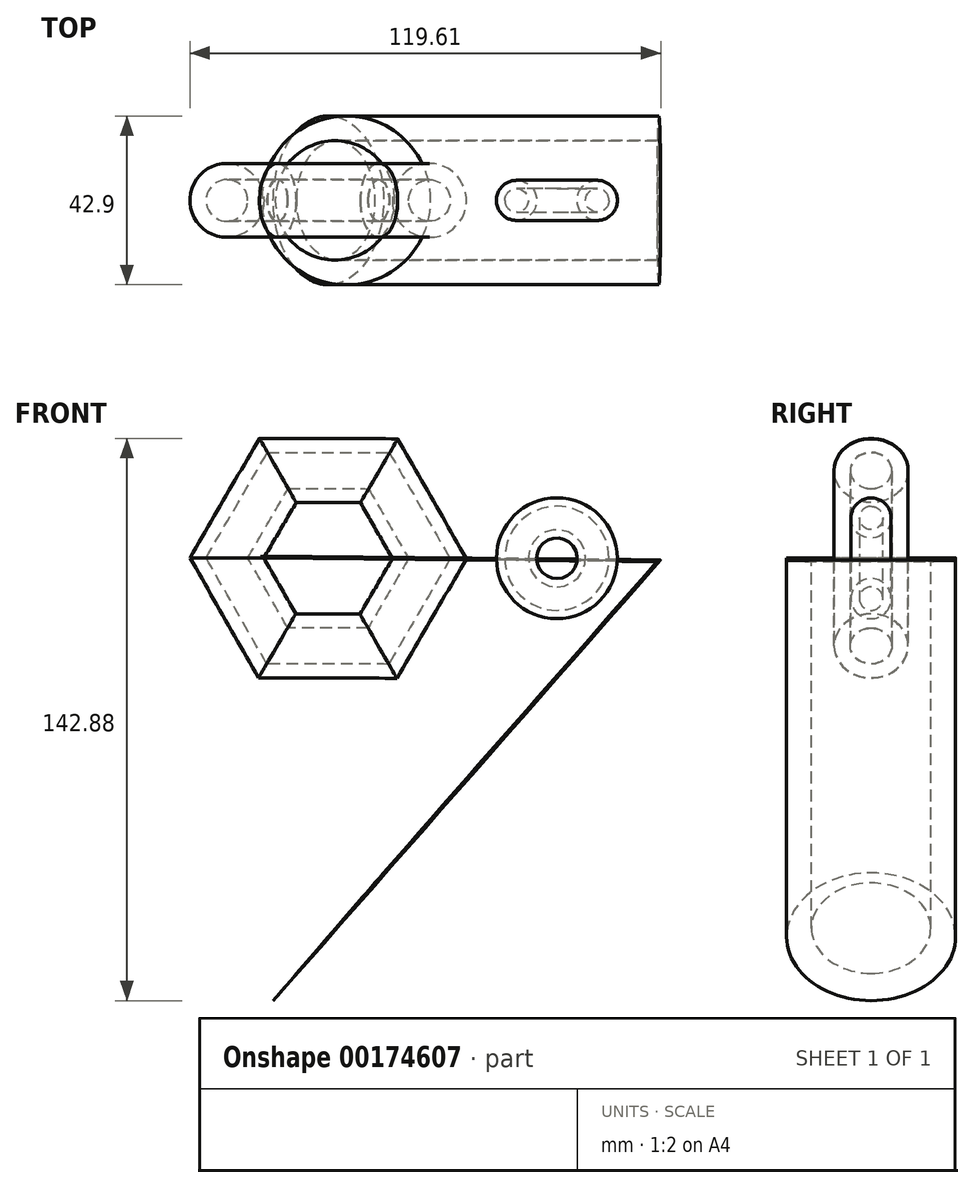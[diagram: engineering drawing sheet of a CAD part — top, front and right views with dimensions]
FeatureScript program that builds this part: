
annotation { "Feature Type Name" : "Feature", "Feature Type Description" : "" }
export const myFeature = defineFeature(function(context is Context, id is Id, definition is map)
    precondition{}
    {
        {
            var Q0;
            Q0=qCreatedBy(makeId("Front.planeOp"),FACE);
            var sketch = newSketch(context, id + "F0", { "sketchPlane" : qUnion([Q0])});
            skCircle(sketch, "E0.cCircle", {"center": v(0, 0) * mm, "radius": 22.68 * mm, "construction": true});
            skLineSegment(sketch, "E0.0", {"start": v(13.18, 22.63) * mm, "end": v(26.19, -0.1) * mm});
            skLineSegment(sketch, "E0.1", {"start": v(26.19, -0.1) * mm, "end": v(13.01, -22.73) * mm});
            skLineSegment(sketch, "E0.2", {"start": v(13.01, -22.73) * mm, "end": v(-13.18, -22.63) * mm});
            skLineSegment(sketch, "E0.3", {"start": v(-13.18, -22.63) * mm, "end": v(-26.19, 0.1) * mm});
            skLineSegment(sketch, "E0.4", {"start": v(-26.19, 0.1) * mm, "end": v(-13.01, 22.73) * mm});
            skLineSegment(sketch, "E0.5", {"start": v(-13.01, 22.73) * mm, "end": v(13.18, 22.63) * mm});
            skPoint(sketch, "E0.0.midPoint", {"position": v(19.68, 11.27) * mm});
            skSolve(sketch);
        }
        {
            var Q0;
            Q0=qCreatedBy(makeId("Top.planeOp"),FACE);
            var sketch = newSketch(context, id + "F1", { "sketchPlane" : qUnion([Q0])});
            skCircle(sketch, "E1", {"center": v(-25.67, 0) * mm, "radius": 9.38 * mm});
            skCircle(sketch, "E2", {"center": v(-25.67, 0) * mm, "radius": 5.28 * mm});
            skSolve(sketch);
        }
        {
            var Q0;
            Q0=makeQuery(id+"F1.imprint","IMPRINT",FACE,{"disambiguationData":[TD([[makeQuery(id+"F1.imprint","IMPRINT",EDGE,{"derivedFrom":sQuery(id+"F1.wireOp",EDGE,"E1")}),1.0]])]});
            var Q1;
            Q1=sQuery(id+"F0.wireOp",EDGE,"E0.4");
            var Q2;
            Q2=sQuery(id+"F0.wireOp",EDGE,"E0.5");
            var Q3;
            Q3=sQuery(id+"F0.wireOp",EDGE,"E0.0");
            var Q4;
            Q4=sQuery(id+"F0.wireOp",EDGE,"E0.1");
            var Q5;
            Q5=sQuery(id+"F0.wireOp",EDGE,"E0.2");
            var Q6;
            Q6=sQuery(id+"F0.wireOp",EDGE,"E0.3");
            sweep(context, id + "F2", {"profiles" : qUnion([Q0]), "path" : qUnion([Q1, Q2, Q3, Q4, Q5, Q6])});
        }
        {
            var Q0;
            Q0=qCreatedBy(makeId("Front.planeOp"),FACE);
            var sketch = newSketch(context, id + "F3", { "sketchPlane" : qUnion([Q0])});
            skCircle(sketch, "E3", {"center": v(58.11, 0) * mm, "radius": 12.49 * mm});
            skCircle(sketch, "E4", {"center": v(58.11, 0) * mm, "radius": 5.1 * mm});
            skSolve(sketch);
        }
        {
            var Q0;
            Q0=qCreatedBy(makeId("Top.planeOp"),FACE);
            var sketch = newSketch(context, id + "F4", { "sketchPlane" : qUnion([Q0])});
            skCircle(sketch, "E5", {"center": v(68.36, 0) * mm, "radius": 5.1 * mm});
            skCircle(sketch, "E6", {"center": v(68.36, 0) * mm, "radius": 2.98 * mm});
            skSolve(sketch);
        }
        {
            var Q0;
            Q0=makeQuery(id+"F4.imprint","IMPRINT",FACE,{"disambiguationData":[TD([[makeQuery(id+"F4.imprint","IMPRINT",EDGE,{"derivedFrom":sQuery(id+"F4.wireOp",EDGE,"E5")}),1.0]])]});
            var Q1;
            Q1=sQuery(id+"F3.wireOp",EDGE,"E3");
            sweep(context, id + "F5", {"profiles" : qUnion([Q0]), "path" : qUnion([Q1])});
        }
        {
            var Q0;
            Q0=qCreatedBy(makeId("Front.planeOp"),FACE);
            var sketch = newSketch(context, id + "F6", { "sketchPlane" : qUnion([Q0])});
            skLineSegment(sketch, "E7", {"start": v(16.81, -30.67) * mm, "end": v(-8.8, -59.8) * mm});
            skLineSegment(sketch, "E8", {"start": v(-8.8, -59.8) * mm, "end": v(-17.13, -30.35) * mm});
            skLineSegment(sketch, "E9", {"start": v(-17.13, -30.35) * mm, "end": v(16.81, -30.67) * mm});
            skSolve(sketch);
        }
        {
            var Q0;
            Q0=qCreatedBy(makeId("Top.planeOp"),FACE);
            var sketch = newSketch(context, id + "F7", { "sketchPlane" : qUnion([Q0])});
            skCircle(sketch, "E10", {"center": v(16.17, 0) * mm, "radius": 21.45 * mm});
            skCircle(sketch, "E11", {"center": v(13.3, 0) * mm, "radius": 15.16 * mm});
            skSolve(sketch);
        }
        {
            var Q0;
            Q0=makeQuery(id+"F7.imprint","IMPRINT",FACE,{"disambiguationData":[TD([[makeQuery(id+"F7.imprint","IMPRINT",EDGE,{"derivedFrom":sQuery(id+"F7.wireOp",EDGE,"E10")}),1.0]])]});
            var Q1;
            Q1=sQuery(id+"F6.wireOp",EDGE,"E7");
            var Q2;
            Q2=sQuery(id+"F6.wireOp",EDGE,"E9");
            sweep(context, id + "F8", {"profiles" : qUnion([Q0]), "path" : qUnion([Q1, Q2])});
        }
    });
